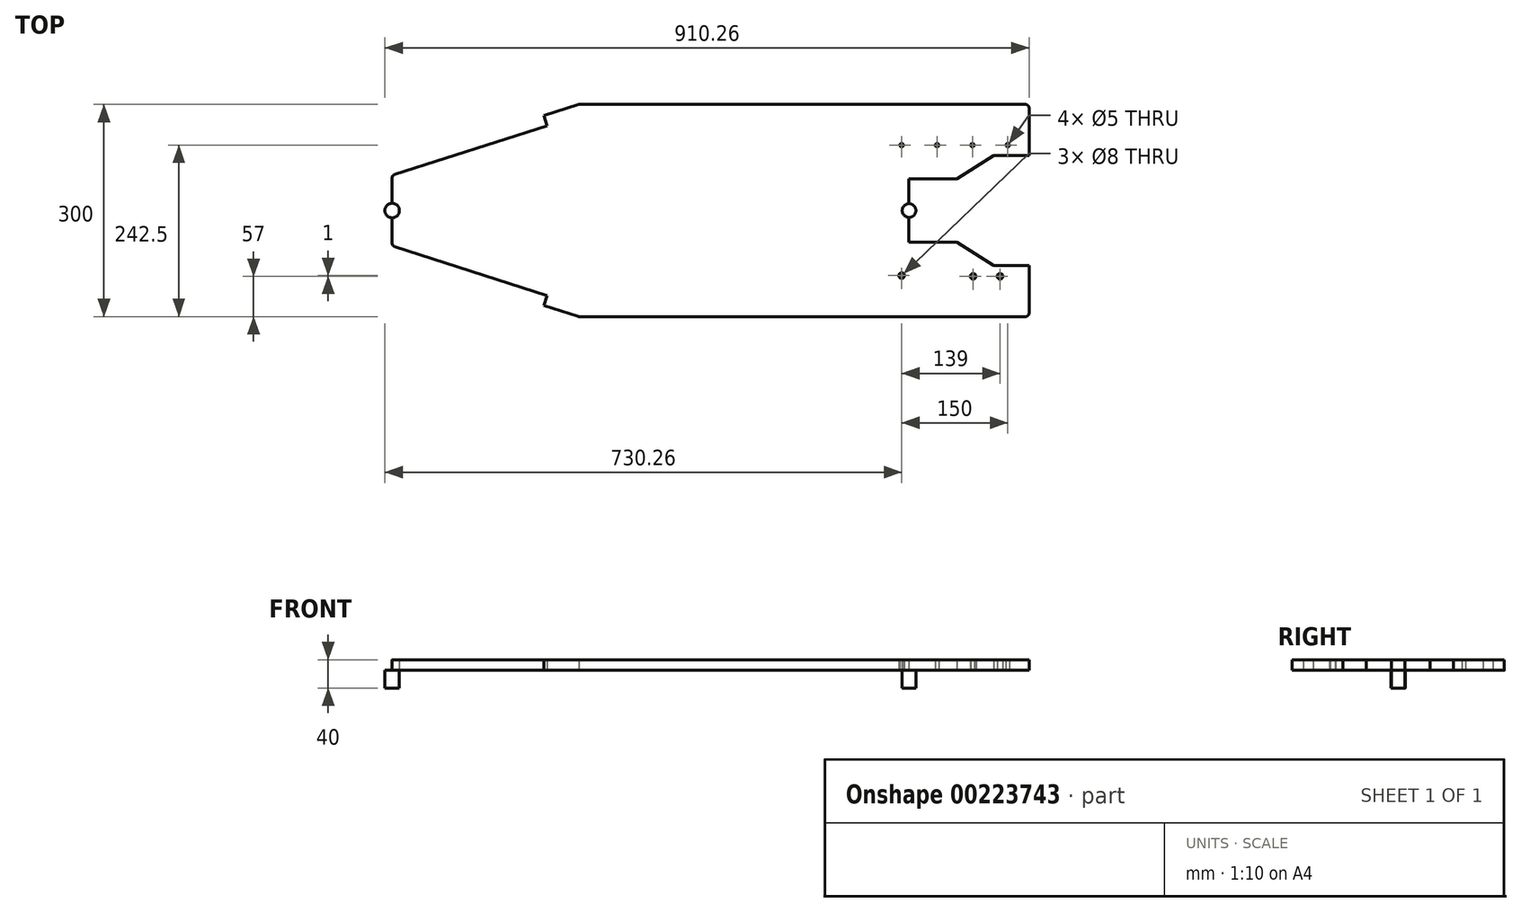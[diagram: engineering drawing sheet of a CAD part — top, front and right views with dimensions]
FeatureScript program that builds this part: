
annotation { "Feature Type Name" : "Feature", "Feature Type Description" : "" }
export const myFeature = defineFeature(function(context is Context, id is Id, definition is map)
    precondition{}
    {
        {
            var Q0;
            Q0=qCreatedBy(makeId("Top.planeOp"),FACE);
            var sketch = newSketch(context, id + "F0", { "sketchPlane" : qUnion([Q0])});
            skLineSegment(sketch, "E0", {"start": v(-190.18, 0) * mm, "end": v(860, 0) * mm, "construction": true});
            skLineSegment(sketch, "E1", {"start": v(0, 0) * mm, "end": v(0, 50) * mm});
            skLineSegment(sketch, "E2", {"start": v(0, 50) * mm, "end": v(219.09, 120) * mm});
            skLineSegment(sketch, "E3", {"start": v(219.09, 120) * mm, "end": v(214.52, 134.29) * mm});
            skLineSegment(sketch, "E4", {"start": v(214.52, 134.29) * mm, "end": v(263.7, 150) * mm});
            skLineSegment(sketch, "E5", {"start": v(263.7, 150) * mm, "end": v(900, 150) * mm});
            skLineSegment(sketch, "E6", {"start": v(900, 150) * mm, "end": v(900, 78) * mm});
            skCircle(sketch, "E7", {"center": v(785, 0) * mm, "radius": 45 * mm});
            skLineSegment(sketch, "E8.MirrorCS", {"start": v(0, -50) * mm, "end": v(219.09, -120) * mm});
            skLineSegment(sketch, "E9.MirrorCS", {"start": v(219.09, -120) * mm, "end": v(214.52, -134.29) * mm});
            skLineSegment(sketch, "E10.MirrorCS", {"start": v(214.52, -134.29) * mm, "end": v(263.7, -150) * mm});
            skLineSegment(sketch, "E11.MirrorCS", {"start": v(900, -150) * mm, "end": v(900, -78) * mm});
            skCircle(sketch, "E12", {"center": v(720, 92.5) * mm, "radius": 2.5 * mm});
            skCircle(sketch, "E13.1.0.0", {"center": v(770, 92.5) * mm, "radius": 2.5 * mm});
            skCircle(sketch, "E13.2.0.0", {"center": v(820, 92.5) * mm, "radius": 2.5 * mm});
            skCircle(sketch, "E13.3.0.0", {"center": v(870, 92.5) * mm, "radius": 2.5 * mm});
            skLineSegment(sketch, "E13.direction1", {"start": v(720, 92.5) * mm, "end": v(770, 92.5) * mm, "construction": true});
            skCircle(sketch, "E14", {"center": v(720, -92) * mm, "radius": 4 * mm});
            skLineSegment(sketch, "E15", {"start": v(785, 45) * mm, "end": v(785, 45) * mm});
            skLineSegment(sketch, "E16", {"start": v(785, -45) * mm, "end": v(785, -45) * mm});
            skLineSegment(sketch, "E17.MirrorCS", {"start": v(263.7, -150) * mm, "end": v(900, -150) * mm});
            skLineSegment(sketch, "E18.MirrorCS", {"start": v(0, 0) * mm, "end": v(0, -50) * mm});
            skLineSegment(sketch, "E19", {"start": v(900, 78) * mm, "end": v(850, 78) * mm});
            skLineSegment(sketch, "E20", {"start": v(850, 78) * mm, "end": v(797.86, 45) * mm});
            skLineSegment(sketch, "E21", {"start": v(797.86, 45) * mm, "end": v(785, 45) * mm});
            skLineSegment(sketch, "E22.MirrorCS", {"start": v(797.86, -45) * mm, "end": v(785, -45) * mm});
            skLineSegment(sketch, "E23.MirrorCS", {"start": v(850, -78) * mm, "end": v(797.86, -45) * mm});
            skLineSegment(sketch, "E24.MirrorCS", {"start": v(900, -78) * mm, "end": v(850, -78) * mm});
            skLineSegment(sketch, "E25", {"start": v(785, 45) * mm, "end": v(730, 45) * mm});
            skLineSegment(sketch, "E26", {"start": v(730, 45) * mm, "end": v(730, -45) * mm});
            skLineSegment(sketch, "E27", {"start": v(730, -45) * mm, "end": v(785, -45) * mm});
            skCircle(sketch, "E28", {"center": v(859, -93) * mm, "radius": 4 * mm});
            skCircle(sketch, "E29", {"center": v(821, -93) * mm, "radius": 4 * mm});
            skSolve(sketch);
        }
        {
            var Q0;
            Q0=makeQuery(id+"F0.imprint","IMPRINT",FACE,{"disambiguationData":[TD([[makeQuery(id+"F0.imprint","IMPRINT",EDGE,{"derivedFrom":sQuery(id+"F0.wireOp",EDGE,"E1")}),-1.0]])]});
            extrude(context, id + "F1", {"entities" : qUnion([Q0]), "depth" : 15 * mm});
        }
        {
            var Q0;
            Q0=makeQuery(id+"F1.opExtrude","SWEPT_EDGE",EDGE,{"disambiguationData":[OSD([sQuery(id+"F0.wireOp",EDGE,"E16"),sQuery(id+"F0.wireOp",EDGE,"bxKCFWjz-ugWH-aJsk-onC8-qf5qAPAfptVs")])]});
            var Q1;
            Q1=makeQuery(id+"F1.opExtrude","SWEPT_EDGE",EDGE,{"disambiguationData":[OSD([sQuery(id+"F0.wireOp",EDGE,"E15"),sQuery(id+"F0.wireOp",EDGE,"vFAnZy5b-keOG-HvUk-P3ux-aojRlNcSxbHs")])]});
            var Q2;
            Q2=makeQuery(id+"F1.opExtrude","SWEPT_EDGE",EDGE,{"disambiguationData":[OSD([sQuery(id+"F0.wireOp",EDGE,"E10.MirrorCS"),sQuery(id+"F0.wireOp",EDGE,"E17.MirrorCS")])]});
            fillet(context, id + "F2", {"entities" : qUnion([Q0, Q1, Q2]), "radius" : 5 * mm, "tangentPropagation" : true, "allowEdgeOverflow" : false});
        }
        {
            var Q0;
            Q0=makeQuery(id+"F1.opExtrude","SWEPT_EDGE",EDGE,{"disambiguationData":[OSD([sQuery(id+"F0.wireOp",EDGE,"E8.MirrorCS"),sQuery(id+"F0.wireOp",EDGE,"E18.MirrorCS")])]});
            var Q1;
            Q1=makeQuery(id+"F1.opExtrude","SWEPT_EDGE",EDGE,{"disambiguationData":[OSD([sQuery(id+"F0.wireOp",EDGE,"E1"),sQuery(id+"F0.wireOp",EDGE,"E2")])]});
            fillet(context, id + "F3", {"entities" : qUnion([Q0, Q1]), "radius" : 5 * mm, "tangentPropagation" : true, "allowEdgeOverflow" : false});
        }
        {
            var Q0;
            Q0=makeQuery(id+"F1.opExtrude","SWEPT_EDGE",EDGE,{"disambiguationData":[OSD([sQuery(id+"F0.wireOp",EDGE,"E5"),sQuery(id+"F0.wireOp",EDGE,"E6")])]});
            var Q1;
            Q1=makeQuery(id+"F1.opExtrude","SWEPT_EDGE",EDGE,{"disambiguationData":[OSD([sQuery(id+"F0.wireOp",EDGE,"E11.MirrorCS"),sQuery(id+"F0.wireOp",EDGE,"E17.MirrorCS")])]});
            fillet(context, id + "F4", {"entities" : qUnion([Q0, Q1]), "radius" : 5 * mm, "tangentPropagation" : true, "allowEdgeOverflow" : false});
        }
        {
            var Q0;
            Q0=qCreatedBy(makeId("Top.planeOp"),FACE);
            var sketch = newSketch(context, id + "F5", { "sketchPlane" : qUnion([Q0])});
            skCircle(sketch, "E30", {"center": v(0, 0) * mm, "radius": 10.26 * mm});
            skCircle(sketch, "E31", {"center": v(730.38, 0) * mm, "radius": 9.68 * mm});
            skSolve(sketch);
        }
        {
            var Q0;
            Q0=qSketchRegion(id+"F5",true);
            extrude(context, id + "F6", {"entities" : qUnion([Q0]), "operationType" : NewBodyOperationType.REMOVE, "depth" : 25 * mm});
        }
        {
            var Q0;
            Q0=qSketchRegion(id+"F5",true);
            extrude(context, id + "F7", {"entities" : qUnion([Q0]), "operationType" : NewBodyOperationType.ADD, "oppositeDirection" : true, "depth" : 25 * mm});
        }
    });
